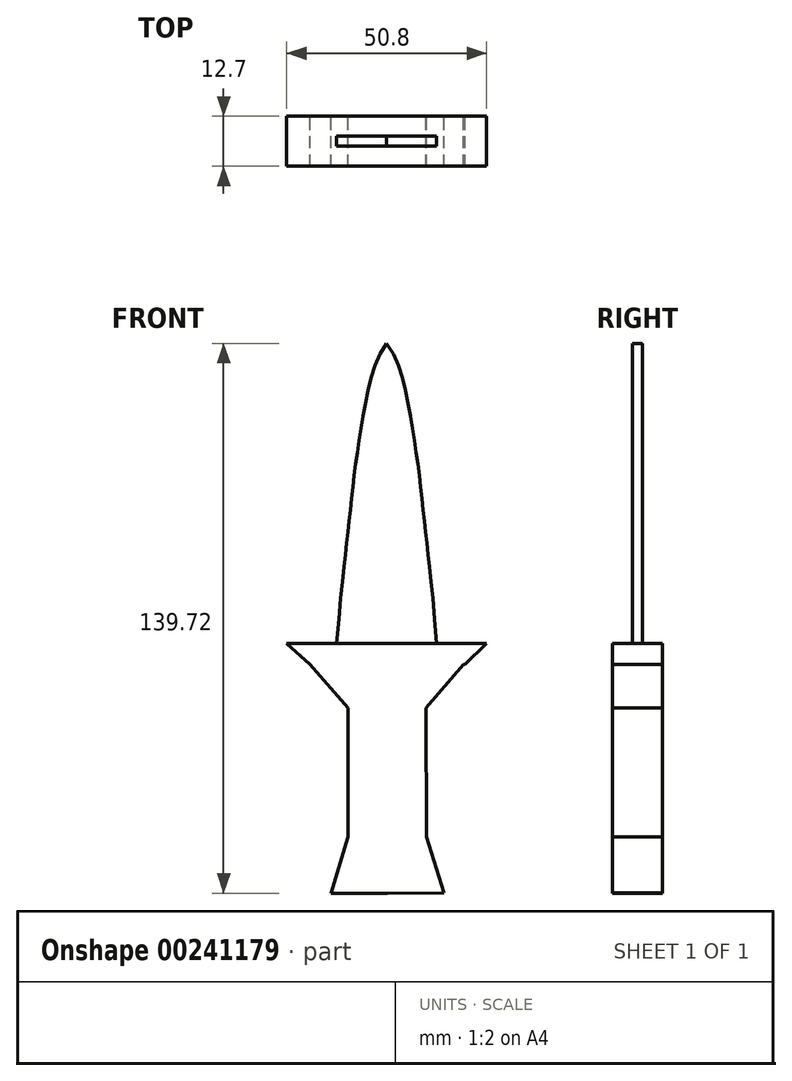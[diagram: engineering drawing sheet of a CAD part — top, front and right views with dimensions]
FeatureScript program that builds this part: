
annotation { "Feature Type Name" : "Feature", "Feature Type Description" : "" }
export const myFeature = defineFeature(function(context is Context, id is Id, definition is map)
    precondition{}
    {
        {
            var Q0;
            Q0=qCreatedBy(makeId("Front.planeOp"),FACE);
            var sketch = newSketch(context, id + "F0", { "sketchPlane" : qUnion([Q0])});
            skLineSegment(sketch, "E0", {"start": v(0, 76.2) * mm, "end": v(0, 0) * mm});
            skFitSpline(sketch, "E1", {"points": [v(0, 76.2) * mm, v(5.81, 58.93) * mm, v(8.25, 42.7) * mm, v(9.87, 28.38) * mm, v(12.7, 0) * mm], "startDerivative": vector(42.63, -58.09) * mm, "endDerivative": vector(12.84, -154.88) * mm});
            skLineSegment(sketch, "E2", {"start": v(12.7, 0) * mm, "end": v(25.4, 0) * mm});
            skLineSegment(sketch, "E3", {"start": v(12.7, 0) * mm, "end": v(0, 0) * mm});
            skLineSegment(sketch, "E4", {"start": v(0, 0) * mm, "end": v(-25.4, 0) * mm});
            skLineSegment(sketch, "E5", {"start": v(-25.4, 0) * mm, "end": v(-19.53, -5.4) * mm});
            skLineSegment(sketch, "E6", {"start": v(-19.53, -5.4) * mm, "end": v(19.87, -5.4) * mm});
            skLineSegment(sketch, "E7", {"start": v(19.87, -5.4) * mm, "end": v(25.4, 0) * mm});
            skFitSpline(sketch, "E8.MirrorCS", {"points": [v(0, 76.2) * mm, v(-5.81, 58.93) * mm, v(-8.25, 42.7) * mm, v(-9.87, 28.38) * mm, v(-12.7, 0) * mm], "startDerivative": vector(-42.63, -58.09) * mm, "endDerivative": vector(-12.84, -154.88) * mm});
            skLineSegment(sketch, "E9", {"start": v(0, 0) * mm, "end": v(0.17, -63.52) * mm});
            skPoint(sketch, "E9.endSnap0", {"position": v(0.17, -5.4) * mm});
            skLineSegment(sketch, "E10", {"start": v(-19.53, -5.4) * mm, "end": v(-9.87, -16.49) * mm});
            skLineSegment(sketch, "E11", {"start": v(-9.87, -16.49) * mm, "end": v(-9.87, -49.2) * mm});
            skLineSegment(sketch, "E12", {"start": v(-9.87, -49.2) * mm, "end": v(-14.2, -63.52) * mm});
            skLineSegment(sketch, "E13", {"start": v(-14.2, -63.52) * mm, "end": v(0.17, -63.52) * mm});
            skLineSegment(sketch, "E14.MirrorCS", {"start": v(9.96, -16.44) * mm, "end": v(10.13, -49.14) * mm});
            skLineSegment(sketch, "E15.MirrorCS", {"start": v(19.56, -5.3) * mm, "end": v(9.96, -16.44) * mm});
            skLineSegment(sketch, "E16.MirrorCS", {"start": v(10.13, -49.14) * mm, "end": v(14.53, -63.45) * mm});
            skLineSegment(sketch, "E17.MirrorCS", {"start": v(14.53, -63.45) * mm, "end": v(0.17, -63.52) * mm});
            skSolve(sketch);
        }
        {
            var Q0;
            {var subQ1=sQuery(id+"F0.wireOp",EDGE,"E5");Q0=makeQuery(id+"F0.imprint","IMPRINT",FACE,{"disambiguationData":[TD([[makeQuery(id+"F0.imprint","IMPRINT",EDGE,{"derivedFrom":subQ1}),1.0]])]});}
            var Q1;
            Q1=makeQuery(id+"F0.imprint","IMPRINT",FACE,{"disambiguationData":[TD([[makeQuery(id+"F0.imprint","IMPRINT",EDGE,{"derivedFrom":sQuery(id+"F0.wireOp",EDGE,"E2")}),-1.0]])]});
            var Q2;
            {var subQ1=sQuery(id+"F0.wireOp",EDGE,"E14.MirrorCS");Q2=makeQuery(id+"F0.imprint","IMPRINT",FACE,{"disambiguationData":[TD([[makeQuery(id+"F0.imprint","IMPRINT",EDGE,{"derivedFrom":subQ1}),-1.0]])]});}
            var Q3;
            {var subQ0=sQuery(id+"F0.wireOp",EDGE,"E10");Q3=makeQuery(id+"F0.imprint","IMPRINT",FACE,{"disambiguationData":[TD([[makeQuery(id+"F0.imprint","IMPRINT",EDGE,{"derivedFrom":subQ0}),1.0]])]});}
            extrude(context, id + "F1", {"entities" : qUnion([Q0, Q1, Q2, Q3]), "depth" : 6.35 * mm, "hasSecondDirection" : true, "secondDirectionOppositeDirection" : true, "secondDirectionDepth" : 6.35 * mm});
        }
        {
            var Q0;
            {var subQ0=sQuery(id+"F0.wireOp",EDGE,"E0");Q0=makeQuery(id+"F0.imprint","IMPRINT",FACE,{"disambiguationData":[TD([[makeQuery(id+"F0.imprint","IMPRINT",EDGE,{"derivedFrom":subQ0}),-1.0]])]});}
            var Q1;
            Q1=makeQuery(id+"F0.imprint","IMPRINT",FACE,{"disambiguationData":[TD([[makeQuery(id+"F0.imprint","IMPRINT",EDGE,{"derivedFrom":sQuery(id+"F0.wireOp",EDGE,"E0")}),1.0]])]});
            extrude(context, id + "F2", {"entities" : qUnion([Q0, Q1]), "operationType" : NewBodyOperationType.ADD, "depth" : 1.27 * mm, "hasSecondDirection" : true, "secondDirectionOppositeDirection" : true, "secondDirectionDepth" : 1.27 * mm});
        }
    });
